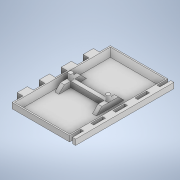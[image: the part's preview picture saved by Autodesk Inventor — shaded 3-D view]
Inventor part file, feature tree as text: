
AUTODESK INVENTOR PART (.ipt)
format: ipt  version: 2020.1 (Build 241239000, 239)  size: 441,344 bytes
history: native  units: mm
features: extrude x9, sketch x9, projected_geometry x6, chamfer x2
ambient origin geometry x8: Origin, YZ Plane, XZ Plane, XY Plane, X Axis, Y Axis, Z Axis, Center Point
bodies: Solid1 (feature_tree)
feature tree (26):
  extrude  "Extrusion1"  Depth=90.0mm
  extrude  "Extrusion2"  Depth=5.419mm
  extrude  "Extrusion3"  Depth=5.419mm
  extrude  "Extrusion4"  Depth=50.0mm
  chamfer  "Chamfer1"  Distance=5.0mm
  extrude  "Tolerances Extrusion "  Depth=3.419mm
  extrude  "Extrusion10"  Depth=2.0mm
  extrude  "Extrusion11"  Depth=4.0mm
  chamfer  "Chamfer3"  Distance=4.0mm
  extrude  "Extrusion12"  Depth=4.0mm
  extrude  "Extrusion13"  Depth=10.0mm
  sketch  "Sketch1"  dims[d0=63.837mm d1=90.0mm]
  sketch  "Sketch2"  dims[d2=5.0mm d3=0.0mm d4=5.419mm]
  sketch  "Sketch3"  dims[d5=10.0mm d6=5.419mm]
  sketch  "Sketch4"  dims[d7=10.0mm d8=50.0mm d10=20.0mm d11=10.0mm d13=10.0mm d15=5.0mm d16=0.0mm]
  projected_geometry  "Projected Loop1"
  sketch  "Sketch9"  dims[d17=90.0mm d18=3.419mm]
  projected_geometry  "Projected Loop10"
  projected_geometry  "Projected Loop11"
  sketch  "Sketch11"  dims[d19=0.0mm d20=2.0mm]
  sketch  "Sketch12"  dims[d21=5.0mm d22=0.0mm d23=5.5mm d24=4.0mm d25=0.0mm]
  projected_geometry  "Projected Loop12"
  sketch  "Sketch13"  dims[d26=4.0mm d27=2.0mm d28=45.0deg d55=0.3mm]
  projected_geometry  "Projected Loop13"
  sketch  "Sketch14"  dims[d56=0.3mm d57=0.3mm d58=0.3mm d59=5.0mm d60=0.0mm d76=3.65mm d77=3.65mm d78=17.05mm d79=17.05mm d80=44.2mm d81=44.2mm d82=10.0mm d83=0.0mm d84=25.0mm d85=25.0mm d86=5.0mm d87=0.0mm d88=5.0mm d89=5.0mm d90=45.0deg d91=2.0mm d92=2.0mm d93=10.0mm d94=0.0mm d95=10.0mm d96=0.0mm d61=0.5mm d62=0.872665mm d63=0.5mm d64=0.872665mm]
  projected_geometry  "Projected Loop14"
